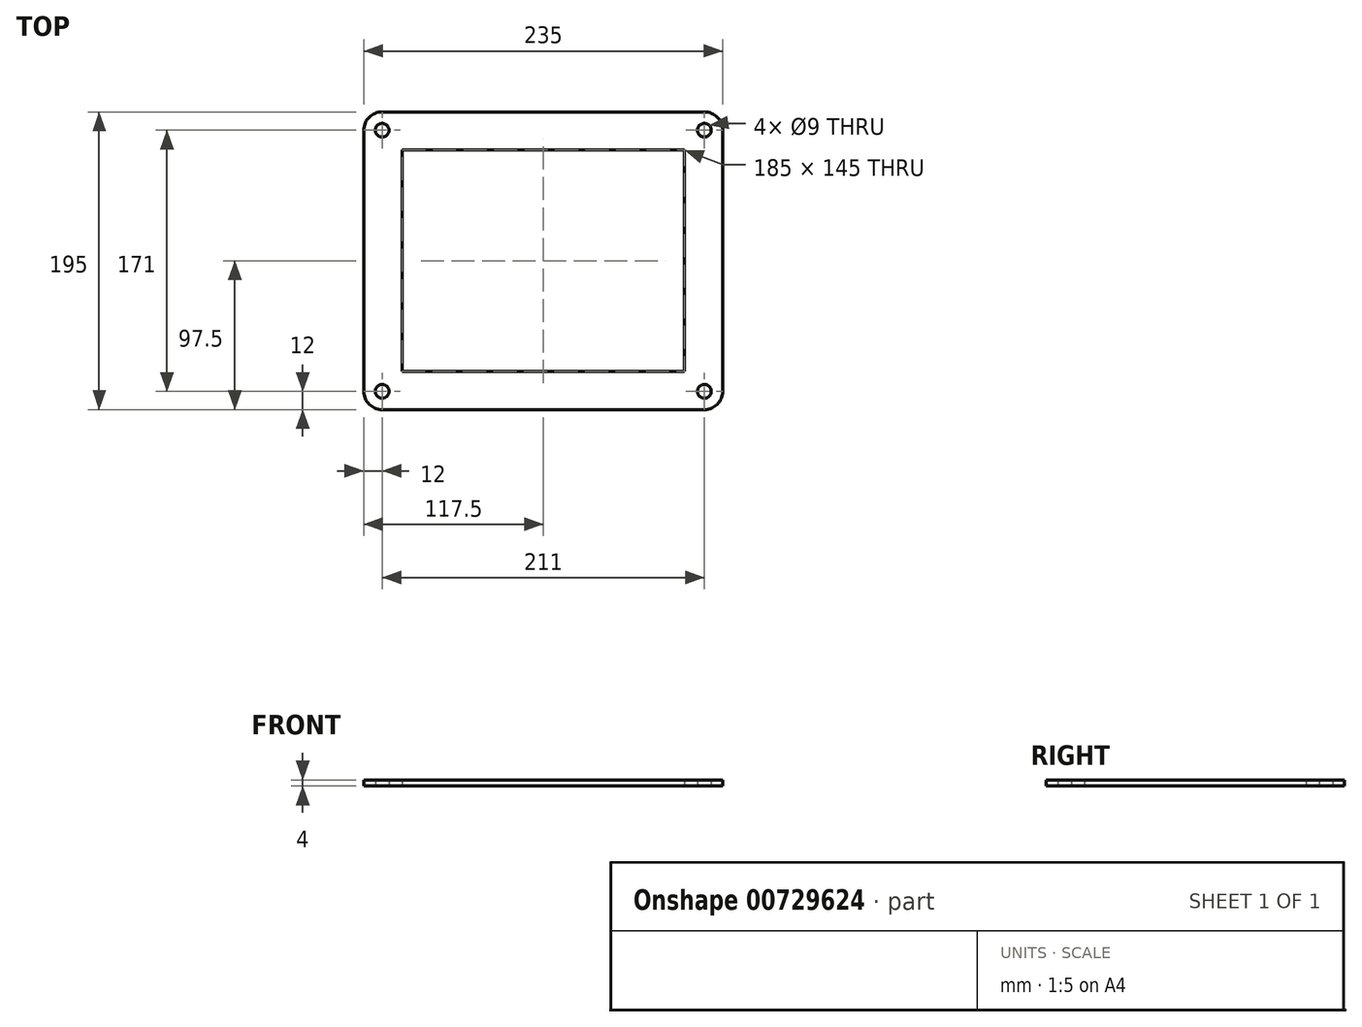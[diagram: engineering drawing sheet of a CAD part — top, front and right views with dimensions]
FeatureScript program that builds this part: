
annotation { "Feature Type Name" : "Feature", "Feature Type Description" : "" }
export const myFeature = defineFeature(function(context is Context, id is Id, definition is map)
    precondition{}
    {
        {
            var Q0;
            Q0=qCreatedBy(makeId("Top.planeOp"),FACE);
            var sketch = newSketch(context, id + "F0", { "sketchPlane" : qUnion([Q0])});
            skLineSegment(sketch, "E0", {"start": v(12, 0) * mm, "end": v(223, 0) * mm});
            skLineSegment(sketch, "E1", {"start": v(235, 12) * mm, "end": v(235, 183) * mm});
            skLineSegment(sketch, "E2", {"start": v(223, 195) * mm, "end": v(12, 195) * mm});
            skLineSegment(sketch, "E3", {"start": v(0, 183) * mm, "end": v(0, 12) * mm});
            skLineSegment(sketch, "E4", {"start": v(25, 170) * mm, "end": v(25, 25) * mm});
            skLineSegment(sketch, "E5", {"start": v(25, 25) * mm, "end": v(210, 25) * mm});
            skLineSegment(sketch, "E6", {"start": v(210, 25) * mm, "end": v(210, 170) * mm});
            skLineSegment(sketch, "E7", {"start": v(210, 170) * mm, "end": v(25, 170) * mm});
            skCircle(sketch, "E8", {"center": v(12, 183) * mm, "radius": 4.5 * mm});
            skCircle(sketch, "E9", {"center": v(223, 183) * mm, "radius": 4.5 * mm});
            skCircle(sketch, "E10", {"center": v(223, 12) * mm, "radius": 4.5 * mm});
            skCircle(sketch, "E11", {"center": v(12, 12) * mm, "radius": 4.5 * mm});
            skPoint(sketch, "E12.visualSharp", {"position": v(0, 195) * mm});
            skArc(sketch, "E12.filletArc", {"start": v(12, 195) * mm, "mid": v(3.51, 191.49) * mm, "end": v(0, 183) * mm});
            skPoint(sketch, "E13.visualSharp", {"position": v(235, 195) * mm});
            skArc(sketch, "E13.filletArc", {"start": v(235, 183) * mm, "mid": v(231.49, 191.49) * mm, "end": v(223, 195) * mm});
            skPoint(sketch, "E14.visualSharp", {"position": v(235, 0) * mm});
            skArc(sketch, "E14.filletArc", {"start": v(223, 0) * mm, "mid": v(231.49, 3.51) * mm, "end": v(235, 12) * mm});
            skPoint(sketch, "E15.visualSharp", {"position": v(0, 0) * mm});
            skArc(sketch, "E15.filletArc", {"start": v(0, 12) * mm, "mid": v(3.51, 3.51) * mm, "end": v(12, 0) * mm});
            skSolve(sketch);
        }
        {
            var Q0;
            Q0=makeQuery(id+"F0.imprint","IMPRINT",FACE,{"disambiguationData":[TD([[makeQuery(id+"F0.imprint","IMPRINT",EDGE,{"derivedFrom":sQuery(id+"F0.wireOp",EDGE,"E0")}),1.0]])]});
            extrude(context, id + "F1", {"entities" : qUnion([Q0]), "depth" : 4 * mm, "offsetDistance" : 25 * mm});
        }
    });
